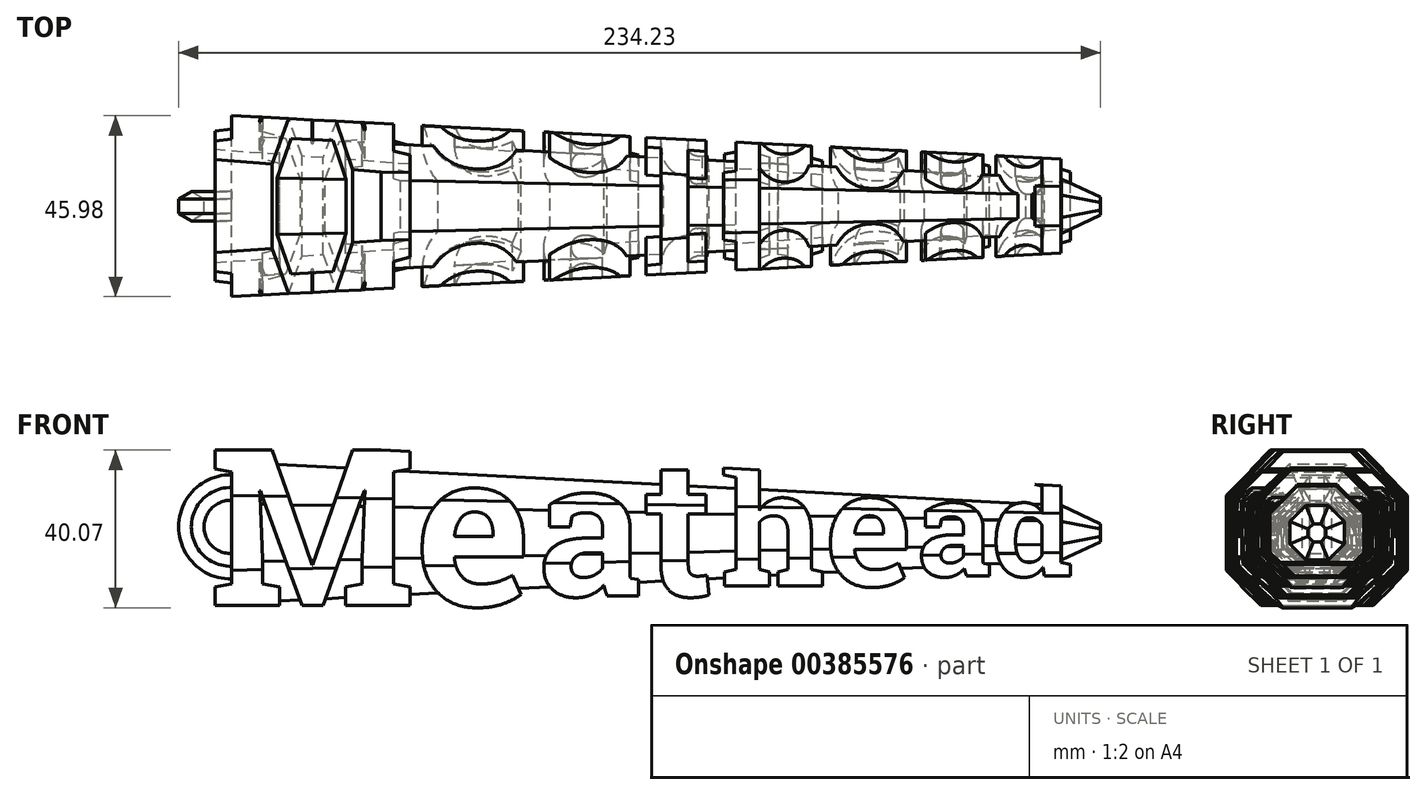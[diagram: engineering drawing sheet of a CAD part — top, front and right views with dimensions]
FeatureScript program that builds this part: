
annotation { "Feature Type Name" : "Feature", "Feature Type Description" : "" }
export const myFeature = defineFeature(function(context is Context, id is Id, definition is map)
    precondition{}
    {
        {
            assignVariable(context, id + "F0", {"name" : "hookPlane", "anyValue" : 105});
        }
        {
            var Q0;
            Q0=qCreatedBy(makeId("Front.planeOp"),FACE);
            var sketch = newSketch(context, id + "F1", { "sketchPlane" : qUnion([Q0])});
            skText(sketch, "E0", { "text": "Me", "fontName": "RobotoSlab-Bold.ttf"});
            skPoint(sketch, "E1", {"position": v(-27.2, 0) * mm});
            skText(sketch, "E2", { "text": "at", "fontName": "RobotoSlab-Bold.ttf"});
            skText(sketch, "E3", { "text": "he", "fontName": "RobotoSlab-Bold.ttf"});
            skText(sketch, "E4", { "text": "ad", "fontName": "RobotoSlab-Bold.ttf"});
            skPoint(sketch, "E5", {"position": v(19.53, 0) * mm});
            skPoint(sketch, "E6", {"position": v(69.24, 0) * mm});
            skLineSegment(sketch, "E7", {"start": v(-110.49, -20) * mm, "end": v(-110.49, -51.65) * mm, "construction": true});
            skLineSegment(sketch, "E8", {"start": v(-110.49, -51.65) * mm, "end": v(110.49, -51.65) * mm, "construction": true});
            skLineSegment(sketch, "E9", {"start": v(110.49, -51.65) * mm, "end": v(110.49, -12.5) * mm, "construction": true});
            skPoint(sketch, "E10", {"position": v(0, -51.65) * mm});
            const initialGuessF1  = {"E0": [-0.11049, -0.02, 1, 0, 0.04], "E2": [-0.0272, -0.0175, 1, 0, 0.035], "E3": [0.01953, -0.015, 1, 0, 0.03], "E4": [0.06924, -0.0125, 1, 0, 0.025]};
            skSetInitialGuess(sketch, initialGuessF1);
            skSolve(sketch);
        }
        {
            var Q0;
            Q0=qSketchRegion(id+"F1",true);
            extrude(context, id + "F2", {"entities" : qUnion([Q0]), "depth" : 25 * mm, "hasSecondDirection" : true, "secondDirectionOppositeDirection" : true, "secondDirectionDepth" : 25 * mm});
        }
        {
            var Q0;
            Q0=qCreatedBy(makeId("Right.planeOp"),FACE);
            var sketch = newSketch(context, id + "F3", { "sketchPlane" : qUnion([Q0])});
            skCircle(sketch, "E11", {"center": v(0, -1.5) * mm, "radius": 12.5 * mm, "construction": true});
            skLineSegment(sketch, "E12", {"start": v(0, 19.5) * mm, "end": v(0, -20) * mm, "construction": true});
            skLineSegment(sketch, "E13.0", {"start": v(-5.18, 11) * mm, "end": v(5.18, 11) * mm});
            skLineSegment(sketch, "E13.1", {"start": v(5.18, 11) * mm, "end": v(12.5, 3.67) * mm});
            skLineSegment(sketch, "E13.2", {"start": v(12.5, 3.67) * mm, "end": v(12.5, -6.68) * mm});
            skLineSegment(sketch, "E13.3", {"start": v(12.5, -6.68) * mm, "end": v(5.18, -14) * mm});
            skLineSegment(sketch, "E13.4", {"start": v(5.18, -14) * mm, "end": v(-5.18, -14) * mm});
            skLineSegment(sketch, "E13.5", {"start": v(-5.18, -14) * mm, "end": v(-12.5, -6.68) * mm});
            skLineSegment(sketch, "E13.6", {"start": v(-12.5, -6.68) * mm, "end": v(-12.5, 3.67) * mm});
            skLineSegment(sketch, "E13.7", {"start": v(-12.5, 3.67) * mm, "end": v(-5.18, 11) * mm});
            skPoint(sketch, "E13.0.midPoint", {"position": v(0, 11) * mm});
            skSolve(sketch);
        }
        {
            var Q0;
            Q0=qSketchRegion(id+"F3",true);
            var Q1;
            Q1=makeQuery(id+"F2.opExtrude","SWEPT_FACE",FACE,{"disambiguationData":[OSD([sQuery(id+"F1.wireOp",EDGE,"E4.sketch_text.stroke-1")])]});
            extrude(context, id + "F4", {"entities" : qUnion([Q0]), "operationType" : NewBodyOperationType.ADD, "oppositeDirection" : true, "depth" : 101 * mm, "hasDraft" : true, "draftAngle" : 3 * degree, "hasSecondDirection" : true, "secondDirectionOppositeDirection" : false, "secondDirectionBoundEntityFace" : qUnion([Q1]), "secondDirectionDepth" : 106 * mm, "hasSecondDirectionDraft" : true, "secondDirectionDraftAngle" : 3 * degree, "secondDirectionDraftPullDirection" : true});
        }
        {
            var Q0;
            Q0=qCreatedBy(makeId("Right.planeOp"),FACE);
            var sketch = newSketch(context, id + "F5", { "sketchPlane" : qUnion([Q0])});
            skCircle(sketch, "E14.cCircle", {"center": v(0, -1.5) * mm, "radius": 17.5 * mm, "construction": true});
            skLineSegment(sketch, "E14.0", {"start": v(-7.25, 16) * mm, "end": v(7.25, 16) * mm});
            skLineSegment(sketch, "E14.1", {"start": v(7.25, 16) * mm, "end": v(17.5, 5.75) * mm});
            skLineSegment(sketch, "E14.2", {"start": v(17.5, 5.75) * mm, "end": v(17.5, -8.75) * mm});
            skLineSegment(sketch, "E14.3", {"start": v(17.5, -8.75) * mm, "end": v(7.25, -19) * mm});
            skLineSegment(sketch, "E14.4", {"start": v(7.25, -19) * mm, "end": v(-7.25, -19) * mm});
            skLineSegment(sketch, "E14.5", {"start": v(-7.25, -19) * mm, "end": v(-17.5, -8.75) * mm});
            skLineSegment(sketch, "E14.6", {"start": v(-17.5, -8.75) * mm, "end": v(-17.5, 5.75) * mm});
            skLineSegment(sketch, "E14.7", {"start": v(-17.5, 5.75) * mm, "end": v(-7.25, 16) * mm});
            skPoint(sketch, "E14.0.midPoint", {"position": v(0, 16) * mm});
            skLineSegment(sketch, "E15.bottom", {"start": v(40.52, 36.35) * mm, "end": v(-40.52, 36.35) * mm});
            skLineSegment(sketch, "E15.top", {"start": v(40.52, -39.36) * mm, "end": v(-40.52, -39.36) * mm});
            skLineSegment(sketch, "E15.left", {"start": v(40.52, 36.35) * mm, "end": v(40.52, -39.36) * mm});
            skLineSegment(sketch, "E15.right", {"start": v(-40.52, 36.35) * mm, "end": v(-40.52, -39.36) * mm});
            skLineSegment(sketch, "E16", {"start": v(0, 19.5) * mm, "end": v(0, -20) * mm, "construction": true});
            skSolve(sketch);
        }
        {
            var Q0;
            Q0=makeQuery(id+"F5.imprint","IMPRINT",FACE,{"disambiguationData":[TD([[makeQuery(id+"F5.imprint","IMPRINT",EDGE,{"derivedFrom":sQuery(id+"F5.wireOp",EDGE,"E14.0")}),1.0]])]});
            extrude(context, id + "F6", {"entities" : qUnion([Q0]), "operationType" : NewBodyOperationType.REMOVE, "endBound" : BoundingType.THROUGH_ALL, "depth" : 25 * mm, "hasDraft" : true, "draftAngle" : 3 * degree, "hasSecondDirection" : true, "secondDirectionBound" : SecondDirectionBoundingType.THROUGH_ALL, "secondDirectionOppositeDirection" : true, "secondDirectionDepth" : 25 * mm, "hasSecondDirectionDraft" : true, "secondDirectionDraftAngle" : 3 * degree, "secondDirectionDraftPullDirection" : true});
        }
        {
            var Q0;
            {var subQ0=sQuery(id+"F3.wireOp",EDGE,"E13.3");var subQ1=sQuery(id+"F3.wireOp",EDGE,"E13.2");var subQ2=sQuery(id+"F3.wireOp",EDGE,"E13.4");var subQ3=sQuery(id+"F3.wireOp",EDGE,"E13.5");var subQ4=sQuery(id+"F3.wireOp",EDGE,"E13.6");Q0=makeQuery(id+"F4.boolean.opBoolean","SPLIT",FACE,{"disambiguationData":[TD([makeQuery(id+"F2.opExtrude","SWEPT_FACE",FACE,{"disambiguationData":[OSD([sQuery(id+"F1.wireOp",EDGE,"E4.sketch_text.stroke-0")])]})])],"derivedFrom":makeQuery(id+"F4.opExtrude","CAP_FACE",FACE,{"disambiguationData":[OSD([sQuery(id+"F3.wireOp",EDGE,"E13.0"),sQuery(id+"F3.wireOp",EDGE,"E13.1"),subQ1,subQ0,subQ2,subQ3,subQ4,sQuery(id+"F3.wireOp",EDGE,"E13.7")])],"isStart":true})});}
            var sketch = newSketch(context, id + "F7", { "sketchPlane" : qUnion([Q0])});
            skCircle(sketch, "E17.cCircle", {"center": v(0, -1.5) * mm, "radius": 6.94 * mm, "construction": true});
            skLineSegment(sketch, "E17.0", {"start": v(-2.88, 5.44) * mm, "end": v(2.88, 5.44) * mm});
            skLineSegment(sketch, "E17.1", {"start": v(2.88, 5.44) * mm, "end": v(6.94, 1.37) * mm});
            skLineSegment(sketch, "E17.2", {"start": v(6.94, 1.37) * mm, "end": v(6.94, -4.38) * mm});
            skLineSegment(sketch, "E17.3", {"start": v(6.94, -4.38) * mm, "end": v(2.88, -8.45) * mm});
            skLineSegment(sketch, "E17.4", {"start": v(2.88, -8.45) * mm, "end": v(-2.88, -8.45) * mm});
            skLineSegment(sketch, "E17.5", {"start": v(-2.88, -8.45) * mm, "end": v(-6.94, -4.38) * mm});
            skLineSegment(sketch, "E17.6", {"start": v(-6.94, -4.38) * mm, "end": v(-6.94, 1.37) * mm});
            skLineSegment(sketch, "E17.7", {"start": v(-6.94, 1.37) * mm, "end": v(-2.88, 5.44) * mm});
            skPoint(sketch, "E17.0.midPoint", {"position": v(0, 5.44) * mm});
            skLineSegment(sketch, "E18", {"start": v(0, 19.59) * mm, "end": v(0, -20.57) * mm, "construction": true});
            skSolve(sketch);
        }
        {
            var Q0;
            Q0=qSketchRegion(id+"F7",true);
            extrude(context, id + "F8", {"entities" : qUnion([Q0]), "operationType" : NewBodyOperationType.ADD, "depth" : 10 * mm, "hasDraft" : true, "draftAngle" : 25 * degree, "draftPullDirection" : true});
        }
        {
            var Q0;
            Q0=qCreatedBy(makeId("Right.planeOp"),FACE);
            cPlane(context, id + "F9", {"entities" : qUnion([Q0]), "cplaneType" : CPlaneType.OFFSET, "offset" : (getVariable(context, 'hookPlane')) * mm, "oppositeDirection" : true, "width" : 150 * mm, "height" : 150 * mm});
        }
        {
            var Q0;
            Q0=qCreatedBy(makeId("Front.planeOp"),FACE);
            var sketch = newSketch(context, id + "F10", { "sketchPlane" : qUnion([Q0])});
            skArc(sketch, "E19", {"start": v(-100, 8.66) * mm, "mid": v(-115, 0) * mm, "end": v(-100, -8.66) * mm});
            skSolve(sketch);
        }
        {
            var Q0;
            Q0=qCreatedBy(id+"F9.planeOp",FACE);
            var sketch = newSketch(context, id + "F11", { "sketchPlane" : qUnion([Q0])});
            skCircle(sketch, "E20.cCircle", {"center": v(0, 10) * mm, "radius": 3.23 * mm, "construction": true});
            skLineSegment(sketch, "E20.0", {"start": v(1.87, 6.77) * mm, "end": v(-1.87, 6.77) * mm});
            skLineSegment(sketch, "E20.1", {"start": v(-1.87, 6.77) * mm, "end": v(-3.73, 10) * mm});
            skLineSegment(sketch, "E20.2", {"start": v(-3.73, 10) * mm, "end": v(-1.87, 13.23) * mm});
            skLineSegment(sketch, "E20.3", {"start": v(-1.87, 13.23) * mm, "end": v(1.87, 13.23) * mm});
            skLineSegment(sketch, "E20.4", {"start": v(1.87, 13.23) * mm, "end": v(3.73, 10) * mm});
            skLineSegment(sketch, "E20.5", {"start": v(3.73, 10) * mm, "end": v(1.87, 6.77) * mm});
            skPoint(sketch, "E20.0.midPoint", {"position": v(0, 6.77) * mm});
            skSolve(sketch);
        }
        {
            var Q0;
            Q0=qSketchRegion(id+"F11",true);
            var Q1;
            Q1=qConstructionFilter(qBodyType(qCreatedBy(id+"F10",EDGE),BodyType.WIRE),ConstructionObject.NO);
            sweep(context, id + "F12", {"operationType" : NewBodyOperationType.ADD, "profiles" : qUnion([Q0]), "path" : qUnion([Q1])});
        }
    });
